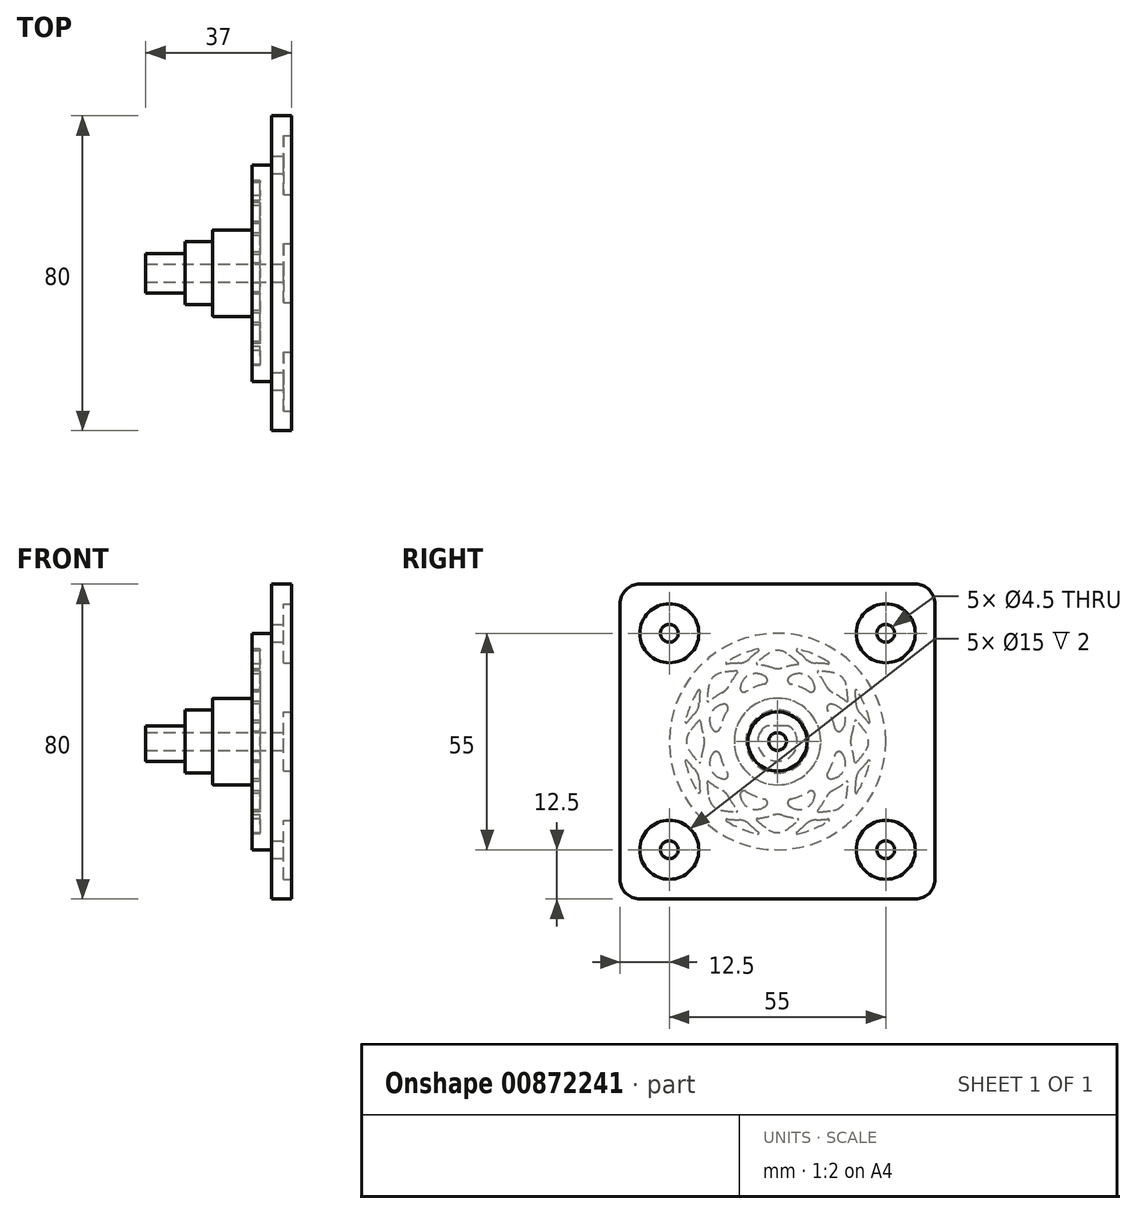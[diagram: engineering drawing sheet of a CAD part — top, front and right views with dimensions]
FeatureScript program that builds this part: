
annotation { "Feature Type Name" : "Feature", "Feature Type Description" : "" }
export const myFeature = defineFeature(function(context is Context, id is Id, definition is map)
    precondition{}
    {
        {
            var Q0;
            Q0=qCreatedBy(makeId("Right.planeOp"),FACE);
            var sketch = newSketch(context, id + "F0", { "sketchPlane" : qUnion([Q0])});
            skCircle(sketch, "E0", {"center": v(0, 0) * mm, "radius": 25 * mm, "construction": true});
            skCircle(sketch, "E1", {"center": v(0, 0) * mm, "radius": 15 * mm, "construction": true});
            skCircle(sketch, "E2", {"center": v(0, 0) * mm, "radius": 8 * mm});
            skArc(sketch, "E3", {"start": v(0, -25) * mm, "mid": v(15, 0) * mm, "end": v(0, 25) * mm, "construction": true});
            skArc(sketch, "E4", {"start": v(0, 25) * mm, "mid": v(-15, 0) * mm, "end": v(0, -25) * mm, "construction": true});
            skArc(sketch, "E5", {"start": v(25, 0) * mm, "mid": v(0, 15) * mm, "end": v(-25, 0) * mm, "construction": true});
            skArc(sketch, "E6", {"start": v(-25, 0) * mm, "mid": v(0, -15) * mm, "end": v(25, 0) * mm, "construction": true});
            skArc(sketch, "E7", {"start": v(17.68, -17.68) * mm, "mid": v(10.6, 10.6) * mm, "end": v(-17.68, 17.68) * mm, "construction": true});
            skArc(sketch, "E8", {"start": v(-17.68, 17.68) * mm, "mid": v(-10.6, -10.6) * mm, "end": v(17.68, -17.68) * mm, "construction": true});
            skArc(sketch, "E9", {"start": v(-17.68, -17.68) * mm, "mid": v(10.6, -10.6) * mm, "end": v(17.68, 17.68) * mm, "construction": true});
            skArc(sketch, "E10", {"start": v(17.68, 17.68) * mm, "mid": v(-10.6, 10.6) * mm, "end": v(-17.68, -17.68) * mm, "construction": true});
            skLineSegment(sketch, "E11", {"start": v(0, 25) * mm, "end": v(0, -25) * mm, "construction": true});
            skLineSegment(sketch, "E12", {"start": v(17.68, 17.68) * mm, "end": v(-17.68, -17.68) * mm, "construction": true});
            skLineSegment(sketch, "E13", {"start": v(-25, 0) * mm, "end": v(25, 0) * mm, "construction": true});
            skLineSegment(sketch, "E14", {"start": v(-17.68, 17.68) * mm, "end": v(17.68, -17.68) * mm, "construction": true});
            skCircle(sketch, "E15", {"center": v(0, 0) * mm, "radius": 27.5 * mm});
            skArc(sketch, "E16", {"start": v(-4, 23.66) * mm, "mid": v(-6.2, 21.88) * mm, "end": v(-8.23, 19.88) * mm});
            skArc(sketch, "E17", {"start": v(-8.23, 19.88) * mm, "mid": v(-11.08, 19.86) * mm, "end": v(-13.9, 19.56) * mm});
            skArc(sketch, "E18", {"start": v(8.23, 19.88) * mm, "mid": v(6.2, 21.88) * mm, "end": v(4, 23.66) * mm});
            skArc(sketch, "E19", {"start": v(16.87, 16.87) * mm, "mid": v(13.42, 17.61) * mm, "end": v(9.9, 17.9) * mm});
            skArc(sketch, "E20", {"start": v(12.97, 12.97) * mm, "mid": v(11.56, 15.51) * mm, "end": v(9.9, 17.9) * mm});
            skArc(sketch, "E21", {"start": v(-19.88, 8.23) * mm, "mid": v(-21.88, 6.2) * mm, "end": v(-23.66, 4) * mm});
            skArc(sketch, "E22", {"start": v(-19.56, 13.9) * mm, "mid": v(-19.86, 11.08) * mm, "end": v(-19.88, 8.23) * mm});
            skArc(sketch, "E23", {"start": v(19.88, 8.23) * mm, "mid": v(19.86, 11.08) * mm, "end": v(19.56, 13.9) * mm});
            skCircle(sketch, "E24", {"center": v(0, 0) * mm, "radius": 11 * mm});
            skArc(sketch, "E25", {"start": v(7.81, 18.86) * mm, "mid": v(4.25, 17.18) * mm, "end": v(1, 14.97) * mm});
            skArc(sketch, "E26", {"start": v(9.88, 11.3) * mm, "mid": v(9.14, 15.16) * mm, "end": v(7.81, 18.86) * mm});
            skArc(sketch, "E27", {"start": v(9.88, 11.3) * mm, "mid": v(5.74, 13.86) * mm, "end": v(1, 14.97) * mm});
            skArc(sketch, "E28", {"start": v(14.97, 1) * mm, "mid": v(17.18, 4.25) * mm, "end": v(18.86, 7.81) * mm});
            skArc(sketch, "E29", {"start": v(18.86, 7.81) * mm, "mid": v(15.16, 9.14) * mm, "end": v(11.3, 9.88) * mm});
            skArc(sketch, "E30", {"start": v(14.97, 1) * mm, "mid": v(13.86, 5.74) * mm, "end": v(11.3, 9.88) * mm});
            skArc(sketch, "E31", {"start": v(-19.66, 5.65) * mm, "mid": v(-21.94, 2.96) * mm, "end": v(-23.86, 0) * mm});
            skArc(sketch, "E32", {"start": v(-23.86, 0) * mm, "mid": v(-21.94, -2.96) * mm, "end": v(-19.66, -5.65) * mm});
            skArc(sketch, "E33", {"start": v(-18.35, 0) * mm, "mid": v(-19.15, -2.8) * mm, "end": v(-19.66, -5.65) * mm});
            skArc(sketch, "E34", {"start": v(23.86, 0) * mm, "mid": v(21.94, 2.96) * mm, "end": v(19.66, 5.65) * mm});
            skArc(sketch, "E35", {"start": v(18.35, 0) * mm, "mid": v(19.15, 2.8) * mm, "end": v(19.66, 5.65) * mm});
            skArc(sketch, "E36", {"start": v(-23.66, -4) * mm, "mid": v(-21.88, -6.2) * mm, "end": v(-19.88, -8.23) * mm});
            skArc(sketch, "E37", {"start": v(-19.88, -8.23) * mm, "mid": v(-19.86, -11.08) * mm, "end": v(-19.56, -13.9) * mm});
            skArc(sketch, "E38", {"start": v(19.88, -8.23) * mm, "mid": v(21.88, -6.2) * mm, "end": v(23.66, -4) * mm});
            skArc(sketch, "E39", {"start": v(19.56, -13.9) * mm, "mid": v(19.86, -11.08) * mm, "end": v(19.88, -8.23) * mm});
            skArc(sketch, "E40", {"start": v(12.97, -12.97) * mm, "mid": v(15.51, -11.56) * mm, "end": v(17.9, -9.9) * mm});
            skArc(sketch, "E41", {"start": v(16.87, -16.87) * mm, "mid": v(17.61, -13.42) * mm, "end": v(17.9, -9.9) * mm});
            skArc(sketch, "E42", {"start": v(-16.87, 16.87) * mm, "mid": v(-17.61, 13.42) * mm, "end": v(-17.9, 9.9) * mm});
            skArc(sketch, "E43", {"start": v(-9.9, 17.9) * mm, "mid": v(-11.56, 15.51) * mm, "end": v(-12.97, 12.97) * mm});
            skArc(sketch, "E44", {"start": v(-9.9, 17.9) * mm, "mid": v(-13.42, 17.61) * mm, "end": v(-16.87, 16.87) * mm});
            skArc(sketch, "E45", {"start": v(-14.97, -1) * mm, "mid": v(-17.18, -4.25) * mm, "end": v(-18.86, -7.81) * mm});
            skArc(sketch, "E46", {"start": v(-18.86, -7.81) * mm, "mid": v(-15.16, -9.14) * mm, "end": v(-11.3, -9.88) * mm});
            skArc(sketch, "E47", {"start": v(-18.86, 7.81) * mm, "mid": v(-17.18, 4.25) * mm, "end": v(-14.97, 1) * mm});
            skArc(sketch, "E48", {"start": v(-11.3, 9.88) * mm, "mid": v(-15.16, 9.14) * mm, "end": v(-18.86, 7.81) * mm});
            skArc(sketch, "E49", {"start": v(-1, 14.97) * mm, "mid": v(-4.25, 17.18) * mm, "end": v(-7.81, 18.86) * mm});
            skArc(sketch, "E50", {"start": v(-7.81, 18.86) * mm, "mid": v(-9.14, 15.16) * mm, "end": v(-9.88, 11.3) * mm});
            skArc(sketch, "E51", {"start": v(-1, 14.97) * mm, "mid": v(-5.74, 13.86) * mm, "end": v(-9.88, 11.3) * mm});
            skArc(sketch, "E52", {"start": v(1, -14.97) * mm, "mid": v(4.25, -17.18) * mm, "end": v(7.81, -18.86) * mm});
            skArc(sketch, "E53", {"start": v(7.81, -18.86) * mm, "mid": v(9.14, -15.16) * mm, "end": v(9.88, -11.3) * mm});
            skArc(sketch, "E54", {"start": v(1, -14.97) * mm, "mid": v(5.74, -13.86) * mm, "end": v(9.88, -11.3) * mm});
            skArc(sketch, "E55", {"start": v(-11.3, 9.88) * mm, "mid": v(-13.86, 5.74) * mm, "end": v(-14.97, 1) * mm});
            skArc(sketch, "E56", {"start": v(-9.88, -11.3) * mm, "mid": v(-9.14, -15.16) * mm, "end": v(-7.81, -18.86) * mm});
            skArc(sketch, "E57", {"start": v(-9.88, -11.3) * mm, "mid": v(-5.74, -13.86) * mm, "end": v(-1, -14.97) * mm});
            skArc(sketch, "E58", {"start": v(18.86, -7.81) * mm, "mid": v(17.18, -4.25) * mm, "end": v(14.97, -1) * mm});
            skArc(sketch, "E59", {"start": v(11.3, -9.88) * mm, "mid": v(15.16, -9.14) * mm, "end": v(18.86, -7.81) * mm});
            skArc(sketch, "E60", {"start": v(11.3, -9.88) * mm, "mid": v(13.86, -5.74) * mm, "end": v(14.97, -1) * mm});
            skArc(sketch, "E61", {"start": v(-7.81, -18.86) * mm, "mid": v(-4.25, -17.18) * mm, "end": v(-1, -14.97) * mm});
            skArc(sketch, "E62", {"start": v(-19.66, 5.65) * mm, "mid": v(-19.15, 2.8) * mm, "end": v(-18.35, 0) * mm});
            skArc(sketch, "E63", {"start": v(-13.9, -19.56) * mm, "mid": v(-11.08, -19.86) * mm, "end": v(-8.23, -19.88) * mm});
            skArc(sketch, "E64", {"start": v(-8.23, -19.88) * mm, "mid": v(-6.2, -21.88) * mm, "end": v(-4, -23.66) * mm});
            skArc(sketch, "E65", {"start": v(-12.97, 12.97) * mm, "mid": v(-15.51, 11.56) * mm, "end": v(-17.9, 9.9) * mm});
            skArc(sketch, "E66", {"start": v(-17.9, -9.9) * mm, "mid": v(-15.51, -11.56) * mm, "end": v(-12.97, -12.97) * mm});
            skArc(sketch, "E67", {"start": v(-17.9, -9.9) * mm, "mid": v(-17.61, -13.42) * mm, "end": v(-16.87, -16.87) * mm});
            skArc(sketch, "E68", {"start": v(-16.87, -16.87) * mm, "mid": v(-13.42, -17.61) * mm, "end": v(-9.9, -17.9) * mm});
            skArc(sketch, "E69", {"start": v(-12.97, -12.97) * mm, "mid": v(-11.56, -15.51) * mm, "end": v(-9.9, -17.9) * mm});
            skArc(sketch, "E70", {"start": v(-5.65, -19.66) * mm, "mid": v(-2.8, -19.15) * mm, "end": v(0, -18.35) * mm});
            skArc(sketch, "E71", {"start": v(-5.65, -19.66) * mm, "mid": v(-2.96, -21.94) * mm, "end": v(0, -23.86) * mm});
            skArc(sketch, "E72", {"start": v(0, -18.35) * mm, "mid": v(2.8, -19.15) * mm, "end": v(5.65, -19.66) * mm});
            skArc(sketch, "E73", {"start": v(0, -23.86) * mm, "mid": v(2.96, -21.94) * mm, "end": v(5.65, -19.66) * mm});
            skArc(sketch, "E74", {"start": v(4, -23.66) * mm, "mid": v(6.2, -21.88) * mm, "end": v(8.23, -19.88) * mm});
            skArc(sketch, "E75", {"start": v(8.23, -19.88) * mm, "mid": v(11.08, -19.86) * mm, "end": v(13.9, -19.56) * mm});
            skArc(sketch, "E76", {"start": v(0, 23.86) * mm, "mid": v(-2.96, 21.94) * mm, "end": v(-5.65, 19.66) * mm});
            skArc(sketch, "E77", {"start": v(0, 18.35) * mm, "mid": v(-2.8, 19.15) * mm, "end": v(-5.65, 19.66) * mm});
            skArc(sketch, "E78", {"start": v(5.65, 19.66) * mm, "mid": v(2.96, 21.94) * mm, "end": v(0, 23.86) * mm});
            skArc(sketch, "E79", {"start": v(5.65, 19.66) * mm, "mid": v(2.8, 19.15) * mm, "end": v(0, 18.35) * mm});
            skArc(sketch, "E80", {"start": v(17.9, 9.9) * mm, "mid": v(15.51, 11.56) * mm, "end": v(12.97, 12.97) * mm});
            skArc(sketch, "E81", {"start": v(17.9, 9.9) * mm, "mid": v(17.61, 13.42) * mm, "end": v(16.87, 16.87) * mm});
            skArc(sketch, "E82", {"start": v(19.66, -5.65) * mm, "mid": v(21.94, -2.96) * mm, "end": v(23.86, 0) * mm});
            skArc(sketch, "E83", {"start": v(19.66, -5.65) * mm, "mid": v(19.15, -2.8) * mm, "end": v(18.35, 0) * mm});
            skArc(sketch, "E84", {"start": v(9.9, -17.9) * mm, "mid": v(11.56, -15.51) * mm, "end": v(12.97, -12.97) * mm});
            skArc(sketch, "E85", {"start": v(9.9, -17.9) * mm, "mid": v(13.42, -17.61) * mm, "end": v(16.87, -16.87) * mm});
            skArc(sketch, "E86", {"start": v(-14.97, -1) * mm, "mid": v(-13.86, -5.74) * mm, "end": v(-11.3, -9.88) * mm});
            skArc(sketch, "E87", {"start": v(-19.56, 13.9) * mm, "mid": v(-22.17, 9.18) * mm, "end": v(-23.66, 4) * mm});
            skCircle(sketch, "E88", {"center": v(0, 0) * mm, "radius": 24 * mm, "construction": true});
            skArc(sketch, "E89", {"start": v(-4, 23.66) * mm, "mid": v(-9.18, 22.17) * mm, "end": v(-13.9, 19.56) * mm});
            skArc(sketch, "E90", {"start": v(23.66, 4) * mm, "mid": v(21.88, 6.2) * mm, "end": v(19.88, 8.23) * mm});
            skArc(sketch, "E91", {"start": v(23.66, 4) * mm, "mid": v(22.17, 9.18) * mm, "end": v(19.56, 13.9) * mm});
            skArc(sketch, "E92", {"start": v(13.9, 19.56) * mm, "mid": v(11.08, 19.86) * mm, "end": v(8.23, 19.88) * mm});
            skArc(sketch, "E93", {"start": v(13.9, 19.56) * mm, "mid": v(9.18, 22.17) * mm, "end": v(4, 23.66) * mm});
            skArc(sketch, "E94", {"start": v(-23.66, -4) * mm, "mid": v(-22.17, -9.18) * mm, "end": v(-19.56, -13.9) * mm});
            skArc(sketch, "E95", {"start": v(-13.9, -19.56) * mm, "mid": v(-9.18, -22.17) * mm, "end": v(-4, -23.66) * mm});
            skArc(sketch, "E96", {"start": v(4, -23.66) * mm, "mid": v(9.18, -22.17) * mm, "end": v(13.9, -19.56) * mm});
            skArc(sketch, "E97", {"start": v(19.56, -13.9) * mm, "mid": v(22.17, -9.18) * mm, "end": v(23.66, -4) * mm});
            skSolve(sketch);
        }
        {
            var Q0;
            Q0=qCreatedBy(makeId("Right.planeOp"),FACE);
            var sketch = newSketch(context, id + "F1", { "sketchPlane" : qUnion([Q0])});
            skCircle(sketch, "E98", {"center": v(0, 0) * mm, "radius": 27.5 * mm});
            skSolve(sketch);
        }
        {
            var Q0;
            Q0 = qSketchRegion(id + "F1", true);
            extrude(context, id + "F2", {"entities" : qUnion([Q0]), "depth" : 5 * mm, "offsetDistance" : 25 * mm});
        }
        {
            var Q0;
            Q0=makeQuery(id+"F2.opExtrude","CAP_FACE",FACE,{"disambiguationData":[OSD([sQuery(id+"F1.wireOp",EDGE,"E98")])],"isStart":false});
            var sketch = newSketch(context, id + "F3", { "sketchPlane" : qUnion([Q0])});
            skLineSegment(sketch, "E99.bottom", {"start": v(40, -40) * mm, "end": v(-40, -40) * mm});
            skLineSegment(sketch, "E99.top", {"start": v(40, 40) * mm, "end": v(-40, 40) * mm});
            skLineSegment(sketch, "E99.left", {"start": v(40, -40) * mm, "end": v(40, 40) * mm});
            skLineSegment(sketch, "E99.right", {"start": v(-40, -40) * mm, "end": v(-40, 40) * mm});
            skPoint(sketch, "E99.middle", {"position": v(0, 0) * mm});
            skSolve(sketch);
        }
        {
            var Q0;
            Q0=makeQuery(id+"F3.imprint","IMPRINT",FACE,{"disambiguationData":[TD([[makeQuery(id+"F3.imprint","IMPRINT",EDGE,{"derivedFrom":sQuery(id+"F3.wireOp",EDGE,"E99.bottom")}),-1.0]])]});
            var Q1;
            Q1=makeQuery(id+"F3.imprint","IMPRINT",FACE,{"disambiguationData":[TD([[makeQuery(id+"F3.imprint","IMPRINT",EDGE,{"derivedFrom":makeQuery(id+"F2.opExtrude","CAP_EDGE",EDGE,{"disambiguationData":[OSD([sQuery(id+"F1.wireOp",EDGE,"E98")])],"isStart":false})}),1.0]])]});
            extrude(context, id + "F4", {"entities" : qUnion([Q0, Q1]), "operationType" : NewBodyOperationType.ADD, "depth" : 5 * mm, "offsetDistance" : 25 * mm});
        }
        {
            var Q0;
            Q0=makeQuery(id+"F0.imprint","IMPRINT",FACE,{"disambiguationData":[TD([[makeQuery(id+"F0.imprint","IMPRINT",EDGE,{"derivedFrom":sQuery(id+"F0.wireOp",EDGE,"E21")}),-1.0]])]});
            var Q1;
            Q1=makeQuery(id+"F0.imprint","IMPRINT",FACE,{"disambiguationData":[TD([[makeQuery(id+"F0.imprint","IMPRINT",EDGE,{"derivedFrom":sQuery(id+"F0.wireOp",EDGE,"E31")}),1.0]])]});
            var Q2;
            Q2=makeQuery(id+"F0.imprint","IMPRINT",FACE,{"disambiguationData":[TD([[makeQuery(id+"F0.imprint","IMPRINT",EDGE,{"derivedFrom":sQuery(id+"F0.wireOp",EDGE,"E47")}),1.0]])]});
            var Q3;
            Q3=makeQuery(id+"F0.imprint","IMPRINT",FACE,{"disambiguationData":[TD([[makeQuery(id+"F0.imprint","IMPRINT",EDGE,{"derivedFrom":sQuery(id+"F0.wireOp",EDGE,"E42")}),1.0]])]});
            var Q4;
            Q4=makeQuery(id+"F0.imprint","IMPRINT",FACE,{"disambiguationData":[TD([[makeQuery(id+"F0.imprint","IMPRINT",EDGE,{"derivedFrom":sQuery(id+"F0.wireOp",EDGE,"E16")}),-1.0]])]});
            var Q5;
            Q5=makeQuery(id+"F0.imprint","IMPRINT",FACE,{"disambiguationData":[TD([[makeQuery(id+"F0.imprint","IMPRINT",EDGE,{"derivedFrom":sQuery(id+"F0.wireOp",EDGE,"E49")}),1.0]])]});
            var Q6;
            Q6=makeQuery(id+"F0.imprint","IMPRINT",FACE,{"disambiguationData":[TD([[makeQuery(id+"F0.imprint","IMPRINT",EDGE,{"derivedFrom":sQuery(id+"F0.wireOp",EDGE,"E76")}),1.0]])]});
            var Q7;
            Q7=makeQuery(id+"F0.imprint","IMPRINT",FACE,{"disambiguationData":[TD([[makeQuery(id+"F0.imprint","IMPRINT",EDGE,{"derivedFrom":sQuery(id+"F0.wireOp",EDGE,"E18")}),-1.0]])]});
            var Q8;
            Q8=makeQuery(id+"F0.imprint","IMPRINT",FACE,{"disambiguationData":[TD([[makeQuery(id+"F0.imprint","IMPRINT",EDGE,{"derivedFrom":sQuery(id+"F0.wireOp",EDGE,"E25")}),1.0]])]});
            var Q9;
            Q9=makeQuery(id+"F0.imprint","IMPRINT",FACE,{"disambiguationData":[TD([[makeQuery(id+"F0.imprint","IMPRINT",EDGE,{"derivedFrom":sQuery(id+"F0.wireOp",EDGE,"E19")}),1.0]])]});
            var Q10;
            Q10=makeQuery(id+"F0.imprint","IMPRINT",FACE,{"disambiguationData":[TD([[makeQuery(id+"F0.imprint","IMPRINT",EDGE,{"derivedFrom":sQuery(id+"F0.wireOp",EDGE,"E23")}),-1.0]])]});
            var Q11;
            Q11=makeQuery(id+"F0.imprint","IMPRINT",FACE,{"disambiguationData":[TD([[makeQuery(id+"F0.imprint","IMPRINT",EDGE,{"derivedFrom":sQuery(id+"F0.wireOp",EDGE,"E28")}),1.0]])]});
            var Q12;
            Q12=makeQuery(id+"F0.imprint","IMPRINT",FACE,{"disambiguationData":[TD([[makeQuery(id+"F0.imprint","IMPRINT",EDGE,{"derivedFrom":sQuery(id+"F0.wireOp",EDGE,"E34")}),1.0]])]});
            var Q13;
            Q13=makeQuery(id+"F0.imprint","IMPRINT",FACE,{"disambiguationData":[TD([[makeQuery(id+"F0.imprint","IMPRINT",EDGE,{"derivedFrom":sQuery(id+"F0.wireOp",EDGE,"E58")}),1.0]])]});
            var Q14;
            Q14=makeQuery(id+"F0.imprint","IMPRINT",FACE,{"disambiguationData":[TD([[makeQuery(id+"F0.imprint","IMPRINT",EDGE,{"derivedFrom":sQuery(id+"F0.wireOp",EDGE,"E40")}),-1.0]])]});
            var Q15;
            Q15=makeQuery(id+"F0.imprint","IMPRINT",FACE,{"disambiguationData":[TD([[makeQuery(id+"F0.imprint","IMPRINT",EDGE,{"derivedFrom":sQuery(id+"F0.wireOp",EDGE,"E38")}),-1.0]])]});
            var Q16;
            Q16=makeQuery(id+"F0.imprint","IMPRINT",FACE,{"disambiguationData":[TD([[makeQuery(id+"F0.imprint","IMPRINT",EDGE,{"derivedFrom":sQuery(id+"F0.wireOp",EDGE,"E74")}),-1.0]])]});
            var Q17;
            Q17=makeQuery(id+"F0.imprint","IMPRINT",FACE,{"disambiguationData":[TD([[makeQuery(id+"F0.imprint","IMPRINT",EDGE,{"derivedFrom":sQuery(id+"F0.wireOp",EDGE,"E52")}),1.0]])]});
            var Q18;
            Q18=makeQuery(id+"F0.imprint","IMPRINT",FACE,{"disambiguationData":[TD([[makeQuery(id+"F0.imprint","IMPRINT",EDGE,{"derivedFrom":sQuery(id+"F0.wireOp",EDGE,"E70")}),-1.0]])]});
            var Q19;
            Q19=makeQuery(id+"F0.imprint","IMPRINT",FACE,{"disambiguationData":[TD([[makeQuery(id+"F0.imprint","IMPRINT",EDGE,{"derivedFrom":sQuery(id+"F0.wireOp",EDGE,"E56")}),1.0]])]});
            var Q20;
            Q20=makeQuery(id+"F0.imprint","IMPRINT",FACE,{"disambiguationData":[TD([[makeQuery(id+"F0.imprint","IMPRINT",EDGE,{"derivedFrom":sQuery(id+"F0.wireOp",EDGE,"E63")}),-1.0]])]});
            var Q21;
            Q21=makeQuery(id+"F0.imprint","IMPRINT",FACE,{"disambiguationData":[TD([[makeQuery(id+"F0.imprint","IMPRINT",EDGE,{"derivedFrom":sQuery(id+"F0.wireOp",EDGE,"E66")}),-1.0]])]});
            var Q22;
            Q22=makeQuery(id+"F0.imprint","IMPRINT",FACE,{"disambiguationData":[TD([[makeQuery(id+"F0.imprint","IMPRINT",EDGE,{"derivedFrom":sQuery(id+"F0.wireOp",EDGE,"E36")}),-1.0]])]});
            var Q23;
            Q23=makeQuery(id+"F0.imprint","IMPRINT",FACE,{"disambiguationData":[TD([[makeQuery(id+"F0.imprint","IMPRINT",EDGE,{"derivedFrom":sQuery(id+"F0.wireOp",EDGE,"E45")}),1.0]])]});
            extrude(context, id + "F5", {"entities" : qUnion([Q0, Q1, Q2, Q3, Q4, Q5, Q6, Q7, Q8, Q9, Q10, Q11, Q12, Q13, Q14, Q15, Q16, Q17, Q18, Q19, Q20, Q21, Q22, Q23]), "operationType" : NewBodyOperationType.REMOVE, "depth" : 2 * mm, "offsetDistance" : 25 * mm});
        }
        {
            var Q0;
            Q0=makeQuery(id+"F5.boolean.opBoolean","COPY",EDGE,{"derivedFrom":makeQuery(id+"F5.opExtrude","SWEPT_EDGE",EDGE,{"disambiguationData":[OSD([sQuery(id+"F0.wireOp",EDGE,"E28"),sQuery(id+"F0.wireOp",EDGE,"E29")])]})});
            var Q1;
            Q1=makeQuery(id+"F5.boolean.opBoolean","COPY",EDGE,{"derivedFrom":makeQuery(id+"F5.opExtrude","SWEPT_EDGE",EDGE,{"disambiguationData":[OSD([sQuery(id+"F0.wireOp",EDGE,"E23"),sQuery(id+"F0.wireOp",EDGE,"E90")])]})});
            var Q2;
            Q2=makeQuery(id+"F5.boolean.opBoolean","COPY",EDGE,{"derivedFrom":makeQuery(id+"F5.opExtrude","SWEPT_EDGE",EDGE,{"disambiguationData":[OSD([sQuery(id+"F0.wireOp",EDGE,"E18"),sQuery(id+"F0.wireOp",EDGE,"E92")])]})});
            var Q3;
            Q3=makeQuery(id+"F5.boolean.opBoolean","COPY",EDGE,{"derivedFrom":makeQuery(id+"F5.opExtrude","SWEPT_EDGE",EDGE,{"disambiguationData":[OSD([sQuery(id+"F0.wireOp",EDGE,"E25"),sQuery(id+"F0.wireOp",EDGE,"E26")])]})});
            var Q4;
            Q4=makeQuery(id+"F5.boolean.opBoolean","COPY",EDGE,{"derivedFrom":makeQuery(id+"F5.opExtrude","SWEPT_EDGE",EDGE,{"disambiguationData":[OSD([sQuery(id+"F0.wireOp",EDGE,"E49"),sQuery(id+"F0.wireOp",EDGE,"E50")])]})});
            var Q5;
            Q5=makeQuery(id+"F5.boolean.opBoolean","COPY",EDGE,{"derivedFrom":makeQuery(id+"F5.opExtrude","SWEPT_EDGE",EDGE,{"disambiguationData":[OSD([sQuery(id+"F0.wireOp",EDGE,"E16"),sQuery(id+"F0.wireOp",EDGE,"E17")])]})});
            var Q6;
            Q6=makeQuery(id+"F5.boolean.opBoolean","COPY",EDGE,{"derivedFrom":makeQuery(id+"F5.opExtrude","SWEPT_EDGE",EDGE,{"disambiguationData":[OSD([sQuery(id+"F0.wireOp",EDGE,"E21"),sQuery(id+"F0.wireOp",EDGE,"E22")])]})});
            var Q7;
            Q7=makeQuery(id+"F5.boolean.opBoolean","COPY",EDGE,{"derivedFrom":makeQuery(id+"F5.opExtrude","SWEPT_EDGE",EDGE,{"disambiguationData":[OSD([sQuery(id+"F0.wireOp",EDGE,"E47"),sQuery(id+"F0.wireOp",EDGE,"E48")])]})});
            var Q8;
            Q8=makeQuery(id+"F5.boolean.opBoolean","COPY",EDGE,{"derivedFrom":makeQuery(id+"F5.opExtrude","SWEPT_EDGE",EDGE,{"disambiguationData":[OSD([sQuery(id+"F0.wireOp",EDGE,"E45"),sQuery(id+"F0.wireOp",EDGE,"E46")])]})});
            var Q9;
            Q9=makeQuery(id+"F5.boolean.opBoolean","COPY",EDGE,{"derivedFrom":makeQuery(id+"F5.opExtrude","SWEPT_EDGE",EDGE,{"disambiguationData":[OSD([sQuery(id+"F0.wireOp",EDGE,"E36"),sQuery(id+"F0.wireOp",EDGE,"E37")])]})});
            var Q10;
            Q10=makeQuery(id+"F5.boolean.opBoolean","COPY",EDGE,{"derivedFrom":makeQuery(id+"F5.opExtrude","SWEPT_EDGE",EDGE,{"disambiguationData":[OSD([sQuery(id+"F0.wireOp",EDGE,"E56"),sQuery(id+"F0.wireOp",EDGE,"E61")])]})});
            var Q11;
            Q11=makeQuery(id+"F5.boolean.opBoolean","COPY",EDGE,{"derivedFrom":makeQuery(id+"F5.opExtrude","SWEPT_EDGE",EDGE,{"disambiguationData":[OSD([sQuery(id+"F0.wireOp",EDGE,"E63"),sQuery(id+"F0.wireOp",EDGE,"E64")])]})});
            var Q12;
            Q12=makeQuery(id+"F5.boolean.opBoolean","COPY",EDGE,{"derivedFrom":makeQuery(id+"F5.opExtrude","SWEPT_EDGE",EDGE,{"disambiguationData":[OSD([sQuery(id+"F0.wireOp",EDGE,"E52"),sQuery(id+"F0.wireOp",EDGE,"E53")])]})});
            var Q13;
            Q13=makeQuery(id+"F5.boolean.opBoolean","COPY",EDGE,{"derivedFrom":makeQuery(id+"F5.opExtrude","SWEPT_EDGE",EDGE,{"disambiguationData":[OSD([sQuery(id+"F0.wireOp",EDGE,"E74"),sQuery(id+"F0.wireOp",EDGE,"E75")])]})});
            var Q14;
            Q14=makeQuery(id+"F5.boolean.opBoolean","COPY",EDGE,{"derivedFrom":makeQuery(id+"F5.opExtrude","SWEPT_EDGE",EDGE,{"disambiguationData":[OSD([sQuery(id+"F0.wireOp",EDGE,"E38"),sQuery(id+"F0.wireOp",EDGE,"E39")])]})});
            var Q15;
            Q15=makeQuery(id+"F5.boolean.opBoolean","COPY",EDGE,{"derivedFrom":makeQuery(id+"F5.opExtrude","SWEPT_EDGE",EDGE,{"disambiguationData":[OSD([sQuery(id+"F0.wireOp",EDGE,"E58"),sQuery(id+"F0.wireOp",EDGE,"E59")])]})});
            var Q16;
            Q16=makeQuery(id+"F5.boolean.opBoolean","COPY",EDGE,{"derivedFrom":makeQuery(id+"F5.opExtrude","SWEPT_EDGE",EDGE,{"disambiguationData":[OSD([sQuery(id+"F0.wireOp",EDGE,"E35"),sQuery(id+"F0.wireOp",EDGE,"E83")])]})});
            var Q17;
            Q17=makeQuery(id+"F5.boolean.opBoolean","COPY",EDGE,{"derivedFrom":makeQuery(id+"F5.opExtrude","SWEPT_EDGE",EDGE,{"disambiguationData":[OSD([sQuery(id+"F0.wireOp",EDGE,"E34"),sQuery(id+"F0.wireOp",EDGE,"E82")])]})});
            var Q18;
            Q18=makeQuery(id+"F5.boolean.opBoolean","COPY",EDGE,{"derivedFrom":makeQuery(id+"F5.opExtrude","SWEPT_EDGE",EDGE,{"disambiguationData":[OSD([sQuery(id+"F0.wireOp",EDGE,"E41"),sQuery(id+"F0.wireOp",EDGE,"E85")])]})});
            var Q19;
            Q19=makeQuery(id+"F5.boolean.opBoolean","COPY",EDGE,{"derivedFrom":makeQuery(id+"F5.opExtrude","SWEPT_EDGE",EDGE,{"disambiguationData":[OSD([sQuery(id+"F0.wireOp",EDGE,"E40"),sQuery(id+"F0.wireOp",EDGE,"E84")])]})});
            var Q20;
            Q20=makeQuery(id+"F5.boolean.opBoolean","COPY",EDGE,{"derivedFrom":makeQuery(id+"F5.opExtrude","SWEPT_EDGE",EDGE,{"disambiguationData":[OSD([sQuery(id+"F0.wireOp",EDGE,"E70"),sQuery(id+"F0.wireOp",EDGE,"E72")])]})});
            var Q21;
            Q21=makeQuery(id+"F5.boolean.opBoolean","COPY",EDGE,{"derivedFrom":makeQuery(id+"F5.opExtrude","SWEPT_EDGE",EDGE,{"disambiguationData":[OSD([sQuery(id+"F0.wireOp",EDGE,"E71"),sQuery(id+"F0.wireOp",EDGE,"E73")])]})});
            var Q22;
            Q22=makeQuery(id+"F5.boolean.opBoolean","COPY",EDGE,{"derivedFrom":makeQuery(id+"F5.opExtrude","SWEPT_EDGE",EDGE,{"disambiguationData":[OSD([sQuery(id+"F0.wireOp",EDGE,"E67"),sQuery(id+"F0.wireOp",EDGE,"E68")])]})});
            var Q23;
            Q23=makeQuery(id+"F5.boolean.opBoolean","COPY",EDGE,{"derivedFrom":makeQuery(id+"F5.opExtrude","SWEPT_EDGE",EDGE,{"disambiguationData":[OSD([sQuery(id+"F0.wireOp",EDGE,"E66"),sQuery(id+"F0.wireOp",EDGE,"E69")])]})});
            var Q24;
            Q24=makeQuery(id+"F5.boolean.opBoolean","COPY",EDGE,{"derivedFrom":makeQuery(id+"F5.opExtrude","SWEPT_EDGE",EDGE,{"disambiguationData":[OSD([sQuery(id+"F0.wireOp",EDGE,"E33"),sQuery(id+"F0.wireOp",EDGE,"E62")])]})});
            var Q25;
            Q25=makeQuery(id+"F5.boolean.opBoolean","COPY",EDGE,{"derivedFrom":makeQuery(id+"F5.opExtrude","SWEPT_EDGE",EDGE,{"disambiguationData":[OSD([sQuery(id+"F0.wireOp",EDGE,"E31"),sQuery(id+"F0.wireOp",EDGE,"E32")])]})});
            var Q26;
            Q26=makeQuery(id+"F5.boolean.opBoolean","COPY",EDGE,{"derivedFrom":makeQuery(id+"F5.opExtrude","SWEPT_EDGE",EDGE,{"disambiguationData":[OSD([sQuery(id+"F0.wireOp",EDGE,"E42"),sQuery(id+"F0.wireOp",EDGE,"E44")])]})});
            var Q27;
            Q27=makeQuery(id+"F5.boolean.opBoolean","COPY",EDGE,{"derivedFrom":makeQuery(id+"F5.opExtrude","SWEPT_EDGE",EDGE,{"disambiguationData":[OSD([sQuery(id+"F0.wireOp",EDGE,"E43"),sQuery(id+"F0.wireOp",EDGE,"E65")])]})});
            var Q28;
            Q28=makeQuery(id+"F5.boolean.opBoolean","COPY",EDGE,{"derivedFrom":makeQuery(id+"F5.opExtrude","SWEPT_EDGE",EDGE,{"disambiguationData":[OSD([sQuery(id+"F0.wireOp",EDGE,"E77"),sQuery(id+"F0.wireOp",EDGE,"E79")])]})});
            var Q29;
            Q29=makeQuery(id+"F5.boolean.opBoolean","COPY",EDGE,{"derivedFrom":makeQuery(id+"F5.opExtrude","SWEPT_EDGE",EDGE,{"disambiguationData":[OSD([sQuery(id+"F0.wireOp",EDGE,"E76"),sQuery(id+"F0.wireOp",EDGE,"E78")])]})});
            var Q30;
            Q30=makeQuery(id+"F5.boolean.opBoolean","COPY",EDGE,{"derivedFrom":makeQuery(id+"F5.opExtrude","SWEPT_EDGE",EDGE,{"disambiguationData":[OSD([sQuery(id+"F0.wireOp",EDGE,"E20"),sQuery(id+"F0.wireOp",EDGE,"E80")])]})});
            var Q31;
            Q31=makeQuery(id+"F5.boolean.opBoolean","COPY",EDGE,{"derivedFrom":makeQuery(id+"F5.opExtrude","SWEPT_EDGE",EDGE,{"disambiguationData":[OSD([sQuery(id+"F0.wireOp",EDGE,"E19"),sQuery(id+"F0.wireOp",EDGE,"E81")])]})});
            fillet(context, id + "F6", {"entities" : qUnion([Q0, Q1, Q2, Q3, Q4, Q5, Q6, Q7, Q8, Q9, Q10, Q11, Q12, Q13, Q14, Q15, Q16, Q17, Q18, Q19, Q20, Q21, Q22, Q23, Q24, Q25, Q26, Q27, Q28, Q29, Q30, Q31]), "radius" : 4 * mm, "tangentPropagation" : true, "defaultsChanged" : false, "vertexSettings" : [], "allowEdgeOverflow" : false});
        }
        {
            var Q0;
            Q0=makeQuery(id+"F5.boolean.opBoolean","COPY",EDGE,{"derivedFrom":makeQuery(id+"F5.opExtrude","SWEPT_EDGE",EDGE,{"disambiguationData":[OSD([sQuery(id+"F0.wireOp",EDGE,"E58"),sQuery(id+"F0.wireOp",EDGE,"E60")])]})});
            var Q1;
            Q1=makeQuery(id+"F5.boolean.opBoolean","COPY",EDGE,{"derivedFrom":makeQuery(id+"F5.opExtrude","SWEPT_EDGE",EDGE,{"disambiguationData":[OSD([sQuery(id+"F0.wireOp",EDGE,"E28"),sQuery(id+"F0.wireOp",EDGE,"E30")])]})});
            var Q2;
            Q2=makeQuery(id+"F5.boolean.opBoolean","COPY",EDGE,{"derivedFrom":makeQuery(id+"F5.opExtrude","SWEPT_EDGE",EDGE,{"disambiguationData":[OSD([sQuery(id+"F0.wireOp",EDGE,"E29"),sQuery(id+"F0.wireOp",EDGE,"E30")])]})});
            var Q3;
            Q3=makeQuery(id+"F5.boolean.opBoolean","COPY",EDGE,{"derivedFrom":makeQuery(id+"F5.opExtrude","SWEPT_EDGE",EDGE,{"disambiguationData":[OSD([sQuery(id+"F0.wireOp",EDGE,"E26"),sQuery(id+"F0.wireOp",EDGE,"E27")])]})});
            var Q4;
            Q4=makeQuery(id+"F5.boolean.opBoolean","COPY",EDGE,{"derivedFrom":makeQuery(id+"F5.opExtrude","SWEPT_EDGE",EDGE,{"disambiguationData":[OSD([sQuery(id+"F0.wireOp",EDGE,"E25"),sQuery(id+"F0.wireOp",EDGE,"E27")])]})});
            var Q5;
            Q5=makeQuery(id+"F5.boolean.opBoolean","COPY",EDGE,{"derivedFrom":makeQuery(id+"F5.opExtrude","SWEPT_EDGE",EDGE,{"disambiguationData":[OSD([sQuery(id+"F0.wireOp",EDGE,"E49"),sQuery(id+"F0.wireOp",EDGE,"E51")])]})});
            var Q6;
            Q6=makeQuery(id+"F5.boolean.opBoolean","COPY",EDGE,{"derivedFrom":makeQuery(id+"F5.opExtrude","SWEPT_EDGE",EDGE,{"disambiguationData":[OSD([sQuery(id+"F0.wireOp",EDGE,"E50"),sQuery(id+"F0.wireOp",EDGE,"E51")])]})});
            var Q7;
            Q7=makeQuery(id+"F5.boolean.opBoolean","COPY",EDGE,{"derivedFrom":makeQuery(id+"F5.opExtrude","SWEPT_EDGE",EDGE,{"disambiguationData":[OSD([sQuery(id+"F0.wireOp",EDGE,"E48"),sQuery(id+"F0.wireOp",EDGE,"E55")])]})});
            var Q8;
            Q8=makeQuery(id+"F5.boolean.opBoolean","COPY",EDGE,{"derivedFrom":makeQuery(id+"F5.opExtrude","SWEPT_EDGE",EDGE,{"disambiguationData":[OSD([sQuery(id+"F0.wireOp",EDGE,"E47"),sQuery(id+"F0.wireOp",EDGE,"E55")])]})});
            var Q9;
            Q9=makeQuery(id+"F5.boolean.opBoolean","COPY",EDGE,{"derivedFrom":makeQuery(id+"F5.opExtrude","SWEPT_EDGE",EDGE,{"disambiguationData":[OSD([sQuery(id+"F0.wireOp",EDGE,"E45"),sQuery(id+"F0.wireOp",EDGE,"E86")])]})});
            var Q10;
            Q10=makeQuery(id+"F5.boolean.opBoolean","COPY",EDGE,{"derivedFrom":makeQuery(id+"F5.opExtrude","SWEPT_EDGE",EDGE,{"disambiguationData":[OSD([sQuery(id+"F0.wireOp",EDGE,"E46"),sQuery(id+"F0.wireOp",EDGE,"E86")])]})});
            var Q11;
            Q11=makeQuery(id+"F5.boolean.opBoolean","COPY",EDGE,{"derivedFrom":makeQuery(id+"F5.opExtrude","SWEPT_EDGE",EDGE,{"disambiguationData":[OSD([sQuery(id+"F0.wireOp",EDGE,"E56"),sQuery(id+"F0.wireOp",EDGE,"E57")])]})});
            var Q12;
            Q12=makeQuery(id+"F5.boolean.opBoolean","COPY",EDGE,{"derivedFrom":makeQuery(id+"F5.opExtrude","SWEPT_EDGE",EDGE,{"disambiguationData":[OSD([sQuery(id+"F0.wireOp",EDGE,"E57"),sQuery(id+"F0.wireOp",EDGE,"E61")])]})});
            var Q13;
            Q13=makeQuery(id+"F5.boolean.opBoolean","COPY",EDGE,{"derivedFrom":makeQuery(id+"F5.opExtrude","SWEPT_EDGE",EDGE,{"disambiguationData":[OSD([sQuery(id+"F0.wireOp",EDGE,"E52"),sQuery(id+"F0.wireOp",EDGE,"E54")])]})});
            var Q14;
            Q14=makeQuery(id+"F5.boolean.opBoolean","COPY",EDGE,{"derivedFrom":makeQuery(id+"F5.opExtrude","SWEPT_EDGE",EDGE,{"disambiguationData":[OSD([sQuery(id+"F0.wireOp",EDGE,"E53"),sQuery(id+"F0.wireOp",EDGE,"E54")])]})});
            var Q15;
            Q15=makeQuery(id+"F5.boolean.opBoolean","COPY",EDGE,{"derivedFrom":makeQuery(id+"F5.opExtrude","SWEPT_EDGE",EDGE,{"disambiguationData":[OSD([sQuery(id+"F0.wireOp",EDGE,"E59"),sQuery(id+"F0.wireOp",EDGE,"E60")])]})});
            fillet(context, id + "F7", {"entities" : qUnion([Q0, Q1, Q2, Q3, Q4, Q5, Q6, Q7, Q8, Q9, Q10, Q11, Q12, Q13, Q14, Q15]), "radius" : 1 * mm, "tangentPropagation" : true, "defaultsChanged" : false, "vertexSettings" : [], "allowEdgeOverflow" : false});
        }
        {
            var Q0;
            Q0=makeQuery(id+"F5.boolean.opBoolean","COPY",EDGE,{"derivedFrom":makeQuery(id+"F5.opExtrude","SWEPT_EDGE",EDGE,{"disambiguationData":[OSD([sQuery(id+"F0.wireOp",EDGE,"E19"),sQuery(id+"F0.wireOp",EDGE,"E20")])]})});
            var Q1;
            Q1=makeQuery(id+"F5.boolean.opBoolean","COPY",EDGE,{"derivedFrom":makeQuery(id+"F5.opExtrude","SWEPT_EDGE",EDGE,{"disambiguationData":[OSD([sQuery(id+"F0.wireOp",EDGE,"E18"),sQuery(id+"F0.wireOp",EDGE,"E93")])]})});
            var Q2;
            Q2=makeQuery(id+"F5.boolean.opBoolean","COPY",EDGE,{"derivedFrom":makeQuery(id+"F5.opExtrude","SWEPT_EDGE",EDGE,{"disambiguationData":[OSD([sQuery(id+"F0.wireOp",EDGE,"E92"),sQuery(id+"F0.wireOp",EDGE,"E93")])]})});
            var Q3;
            Q3=makeQuery(id+"F5.boolean.opBoolean","COPY",EDGE,{"derivedFrom":makeQuery(id+"F5.opExtrude","SWEPT_EDGE",EDGE,{"disambiguationData":[OSD([sQuery(id+"F0.wireOp",EDGE,"E78"),sQuery(id+"F0.wireOp",EDGE,"E79")])]})});
            var Q4;
            Q4=makeQuery(id+"F5.boolean.opBoolean","COPY",EDGE,{"derivedFrom":makeQuery(id+"F5.opExtrude","SWEPT_EDGE",EDGE,{"disambiguationData":[OSD([sQuery(id+"F0.wireOp",EDGE,"E76"),sQuery(id+"F0.wireOp",EDGE,"E77")])]})});
            var Q5;
            Q5=makeQuery(id+"F5.boolean.opBoolean","COPY",EDGE,{"derivedFrom":makeQuery(id+"F5.opExtrude","SWEPT_EDGE",EDGE,{"disambiguationData":[OSD([sQuery(id+"F0.wireOp",EDGE,"E17"),sQuery(id+"F0.wireOp",EDGE,"E89")])]})});
            var Q6;
            Q6=makeQuery(id+"F5.boolean.opBoolean","COPY",EDGE,{"derivedFrom":makeQuery(id+"F5.opExtrude","SWEPT_EDGE",EDGE,{"disambiguationData":[OSD([sQuery(id+"F0.wireOp",EDGE,"E16"),sQuery(id+"F0.wireOp",EDGE,"E89")])]})});
            var Q7;
            Q7=makeQuery(id+"F5.boolean.opBoolean","COPY",EDGE,{"derivedFrom":makeQuery(id+"F5.opExtrude","SWEPT_EDGE",EDGE,{"disambiguationData":[OSD([sQuery(id+"F0.wireOp",EDGE,"E43"),sQuery(id+"F0.wireOp",EDGE,"E44")])]})});
            var Q8;
            Q8=makeQuery(id+"F5.boolean.opBoolean","COPY",EDGE,{"derivedFrom":makeQuery(id+"F5.opExtrude","SWEPT_EDGE",EDGE,{"disambiguationData":[OSD([sQuery(id+"F0.wireOp",EDGE,"E42"),sQuery(id+"F0.wireOp",EDGE,"E65")])]})});
            var Q9;
            Q9=makeQuery(id+"F5.boolean.opBoolean","COPY",EDGE,{"derivedFrom":makeQuery(id+"F5.opExtrude","SWEPT_EDGE",EDGE,{"disambiguationData":[OSD([sQuery(id+"F0.wireOp",EDGE,"E21"),sQuery(id+"F0.wireOp",EDGE,"E87")])]})});
            var Q10;
            Q10=makeQuery(id+"F5.boolean.opBoolean","COPY",EDGE,{"derivedFrom":makeQuery(id+"F5.opExtrude","SWEPT_EDGE",EDGE,{"disambiguationData":[OSD([sQuery(id+"F0.wireOp",EDGE,"E22"),sQuery(id+"F0.wireOp",EDGE,"E87")])]})});
            var Q11;
            Q11=makeQuery(id+"F5.boolean.opBoolean","COPY",EDGE,{"derivedFrom":makeQuery(id+"F5.opExtrude","SWEPT_EDGE",EDGE,{"disambiguationData":[OSD([sQuery(id+"F0.wireOp",EDGE,"E31"),sQuery(id+"F0.wireOp",EDGE,"E62")])]})});
            var Q12;
            Q12=makeQuery(id+"F5.boolean.opBoolean","COPY",EDGE,{"derivedFrom":makeQuery(id+"F5.opExtrude","SWEPT_EDGE",EDGE,{"disambiguationData":[OSD([sQuery(id+"F0.wireOp",EDGE,"E32"),sQuery(id+"F0.wireOp",EDGE,"E33")])]})});
            var Q13;
            Q13=makeQuery(id+"F5.boolean.opBoolean","COPY",EDGE,{"derivedFrom":makeQuery(id+"F5.opExtrude","SWEPT_EDGE",EDGE,{"disambiguationData":[OSD([sQuery(id+"F0.wireOp",EDGE,"E37"),sQuery(id+"F0.wireOp",EDGE,"E94")])]})});
            var Q14;
            Q14=makeQuery(id+"F5.boolean.opBoolean","COPY",EDGE,{"derivedFrom":makeQuery(id+"F5.opExtrude","SWEPT_EDGE",EDGE,{"disambiguationData":[OSD([sQuery(id+"F0.wireOp",EDGE,"E36"),sQuery(id+"F0.wireOp",EDGE,"E94")])]})});
            var Q15;
            Q15=makeQuery(id+"F5.boolean.opBoolean","COPY",EDGE,{"derivedFrom":makeQuery(id+"F5.opExtrude","SWEPT_EDGE",EDGE,{"disambiguationData":[OSD([sQuery(id+"F0.wireOp",EDGE,"E66"),sQuery(id+"F0.wireOp",EDGE,"E67")])]})});
            var Q16;
            Q16=makeQuery(id+"F5.boolean.opBoolean","COPY",EDGE,{"derivedFrom":makeQuery(id+"F5.opExtrude","SWEPT_EDGE",EDGE,{"disambiguationData":[OSD([sQuery(id+"F0.wireOp",EDGE,"E68"),sQuery(id+"F0.wireOp",EDGE,"E69")])]})});
            var Q17;
            Q17=makeQuery(id+"F5.boolean.opBoolean","COPY",EDGE,{"derivedFrom":makeQuery(id+"F5.opExtrude","SWEPT_EDGE",EDGE,{"disambiguationData":[OSD([sQuery(id+"F0.wireOp",EDGE,"E64"),sQuery(id+"F0.wireOp",EDGE,"E95")])]})});
            var Q18;
            Q18=makeQuery(id+"F5.boolean.opBoolean","COPY",EDGE,{"derivedFrom":makeQuery(id+"F5.opExtrude","SWEPT_EDGE",EDGE,{"disambiguationData":[OSD([sQuery(id+"F0.wireOp",EDGE,"E63"),sQuery(id+"F0.wireOp",EDGE,"E95")])]})});
            var Q19;
            Q19=makeQuery(id+"F5.boolean.opBoolean","COPY",EDGE,{"derivedFrom":makeQuery(id+"F5.opExtrude","SWEPT_EDGE",EDGE,{"disambiguationData":[OSD([sQuery(id+"F0.wireOp",EDGE,"E70"),sQuery(id+"F0.wireOp",EDGE,"E71")])]})});
            var Q20;
            Q20=makeQuery(id+"F5.boolean.opBoolean","COPY",EDGE,{"derivedFrom":makeQuery(id+"F5.opExtrude","SWEPT_EDGE",EDGE,{"disambiguationData":[OSD([sQuery(id+"F0.wireOp",EDGE,"E72"),sQuery(id+"F0.wireOp",EDGE,"E73")])]})});
            var Q21;
            Q21=makeQuery(id+"F5.boolean.opBoolean","COPY",EDGE,{"derivedFrom":makeQuery(id+"F5.opExtrude","SWEPT_EDGE",EDGE,{"disambiguationData":[OSD([sQuery(id+"F0.wireOp",EDGE,"E74"),sQuery(id+"F0.wireOp",EDGE,"E96")])]})});
            var Q22;
            Q22=makeQuery(id+"F5.boolean.opBoolean","COPY",EDGE,{"derivedFrom":makeQuery(id+"F5.opExtrude","SWEPT_EDGE",EDGE,{"disambiguationData":[OSD([sQuery(id+"F0.wireOp",EDGE,"E75"),sQuery(id+"F0.wireOp",EDGE,"E96")])]})});
            var Q23;
            Q23=makeQuery(id+"F5.boolean.opBoolean","COPY",EDGE,{"derivedFrom":makeQuery(id+"F5.opExtrude","SWEPT_EDGE",EDGE,{"disambiguationData":[OSD([sQuery(id+"F0.wireOp",EDGE,"E84"),sQuery(id+"F0.wireOp",EDGE,"E85")])]})});
            var Q24;
            Q24=makeQuery(id+"F5.boolean.opBoolean","COPY",EDGE,{"derivedFrom":makeQuery(id+"F5.opExtrude","SWEPT_EDGE",EDGE,{"disambiguationData":[OSD([sQuery(id+"F0.wireOp",EDGE,"E40"),sQuery(id+"F0.wireOp",EDGE,"E41")])]})});
            var Q25;
            Q25=makeQuery(id+"F5.boolean.opBoolean","COPY",EDGE,{"derivedFrom":makeQuery(id+"F5.opExtrude","SWEPT_EDGE",EDGE,{"disambiguationData":[OSD([sQuery(id+"F0.wireOp",EDGE,"E39"),sQuery(id+"F0.wireOp",EDGE,"E97")])]})});
            var Q26;
            Q26=makeQuery(id+"F5.boolean.opBoolean","COPY",EDGE,{"derivedFrom":makeQuery(id+"F5.opExtrude","SWEPT_EDGE",EDGE,{"disambiguationData":[OSD([sQuery(id+"F0.wireOp",EDGE,"E38"),sQuery(id+"F0.wireOp",EDGE,"E97")])]})});
            var Q27;
            Q27=makeQuery(id+"F5.boolean.opBoolean","COPY",EDGE,{"derivedFrom":makeQuery(id+"F5.opExtrude","SWEPT_EDGE",EDGE,{"disambiguationData":[OSD([sQuery(id+"F0.wireOp",EDGE,"E82"),sQuery(id+"F0.wireOp",EDGE,"E83")])]})});
            var Q28;
            Q28=makeQuery(id+"F5.boolean.opBoolean","COPY",EDGE,{"derivedFrom":makeQuery(id+"F5.opExtrude","SWEPT_EDGE",EDGE,{"disambiguationData":[OSD([sQuery(id+"F0.wireOp",EDGE,"E34"),sQuery(id+"F0.wireOp",EDGE,"E35")])]})});
            var Q29;
            Q29=makeQuery(id+"F5.boolean.opBoolean","COPY",EDGE,{"derivedFrom":makeQuery(id+"F5.opExtrude","SWEPT_EDGE",EDGE,{"disambiguationData":[OSD([sQuery(id+"F0.wireOp",EDGE,"E23"),sQuery(id+"F0.wireOp",EDGE,"E91")])]})});
            var Q30;
            Q30=makeQuery(id+"F5.boolean.opBoolean","COPY",EDGE,{"derivedFrom":makeQuery(id+"F5.opExtrude","SWEPT_EDGE",EDGE,{"disambiguationData":[OSD([sQuery(id+"F0.wireOp",EDGE,"E90"),sQuery(id+"F0.wireOp",EDGE,"E91")])]})});
            var Q31;
            Q31=makeQuery(id+"F5.boolean.opBoolean","COPY",EDGE,{"derivedFrom":makeQuery(id+"F5.opExtrude","SWEPT_EDGE",EDGE,{"disambiguationData":[OSD([sQuery(id+"F0.wireOp",EDGE,"E80"),sQuery(id+"F0.wireOp",EDGE,"E81")])]})});
            fillet(context, id + "F8", {"entities" : qUnion([Q0, Q1, Q2, Q3, Q4, Q5, Q6, Q7, Q8, Q9, Q10, Q11, Q12, Q13, Q14, Q15, Q16, Q17, Q18, Q19, Q20, Q21, Q22, Q23, Q24, Q25, Q26, Q27, Q28, Q29, Q30, Q31]), "radius" : 0.25 * mm, "tangentPropagation" : true, "defaultsChanged" : false, "vertexSettings" : [], "allowEdgeOverflow" : false});
        }
        {
            var Q0;
            Q0=makeQuery(id+"F2.opExtrude","CAP_FACE",FACE,{"disambiguationData":[OSD([sQuery(id+"F1.wireOp",EDGE,"E98")])],"isStart":true});
            var sketch = newSketch(context, id + "F9", { "sketchPlane" : qUnion([Q0])});
            skCircle(sketch, "E100", {"center": v(0, 0) * mm, "radius": 11 * mm});
            skCircle(sketch, "E101", {"center": v(0, 0) * mm, "radius": 8 * mm});
            skSolve(sketch);
        }
        {
            var Q0;
            Q0=makeQuery(id+"F9.imprint","IMPRINT",FACE,{"disambiguationData":[TD([[makeQuery(id+"F9.imprint","IMPRINT",EDGE,{"derivedFrom":sQuery(id+"F9.wireOp",EDGE,"E100")}),1.0]])]});
            extrude(context, id + "F10", {"entities" : qUnion([Q0]), "operationType" : NewBodyOperationType.ADD, "depth" : 10 * mm, "offsetDistance" : 25 * mm});
        }
        {
            var Q0;
            Q0=makeQuery(id+"F10.boolean.opBoolean","SPLIT",FACE,{"disambiguationData":[TD([makeQuery(id+"F10.opExtrude","SWEPT_FACE",FACE,{"disambiguationData":[OSD([sQuery(id+"F9.wireOp",EDGE,"E101")])]})])],"derivedFrom":makeQuery(id+"F2.opExtrude","CAP_FACE",FACE,{"disambiguationData":[OSD([sQuery(id+"F1.wireOp",EDGE,"E98")])],"isStart":true})});
            extrude(context, id + "F11", {"entities" : qUnion([Q0]), "operationType" : NewBodyOperationType.ADD, "depth" : 17 * mm, "offsetDistance" : 25 * mm});
        }
        {
            var Q0;
            Q0=makeQuery(id+"F11.opExtrude","CAP_FACE",FACE,{"disambiguationData":[OSD([sQuery(id+"F1.wireOp",EDGE,"E98")])],"isStart":false});
            var sketch = newSketch(context, id + "F12", { "sketchPlane" : qUnion([Q0])});
            skCircle(sketch, "E102", {"center": v(0, 0) * mm, "radius": 5 * mm});
            skLineSegment(sketch, "E103", {"start": v(-3, 4) * mm, "end": v(3, 4) * mm});
            skSolve(sketch);
        }
        {
            var Q0;
            {var subQ0=sQuery(id+"F12.wireOp",EDGE,"E103");Q0=makeQuery(id+"F12.imprint","IMPRINT",FACE,{"disambiguationData":[TD([[makeQuery(id+"F12.imprint","IMPRINT",EDGE,{"derivedFrom":subQ0}),-1.0]])]});}
            extrude(context, id + "F13", {"entities" : qUnion([Q0]), "operationType" : NewBodyOperationType.ADD, "depth" : 10 * mm, "offsetDistance" : 25 * mm});
        }
        {
            var Q0;
            Q0=makeQuery(id+"F4.opExtrude","CAP_FACE",FACE,{"disambiguationData":[OSD([sQuery(id+"F3.wireOp",EDGE,"E99.bottom"),sQuery(id+"F3.wireOp",EDGE,"E99.top"),sQuery(id+"F3.wireOp",EDGE,"E99.left"),sQuery(id+"F3.wireOp",EDGE,"E99.right")])],"isStart":false});
            var sketch = newSketch(context, id + "F14", { "sketchPlane" : qUnion([Q0])});
            skLineSegment(sketch, "E104.bottom", {"start": v(27.5, -27.5) * mm, "end": v(-27.5, -27.5) * mm, "construction": true});
            skLineSegment(sketch, "E104.top", {"start": v(27.5, 27.5) * mm, "end": v(-27.5, 27.5) * mm, "construction": true});
            skLineSegment(sketch, "E104.left", {"start": v(27.5, -27.5) * mm, "end": v(27.5, 27.5) * mm, "construction": true});
            skLineSegment(sketch, "E104.right", {"start": v(-27.5, -27.5) * mm, "end": v(-27.5, 27.5) * mm, "construction": true});
            skPoint(sketch, "E104.middle", {"position": v(0, 0) * mm});
            skSolve(sketch);
        }
        {
            var Q0;
            Q0=sQuery(id+"F14.wireOp",VERTEX,"E104.top.end");
            var Q1;
            Q1=sQuery(id+"F14.wireOp",VERTEX,"E104.bottom.end");
            var Q2;
            Q2=sQuery(id+"F14.wireOp",VERTEX,"E104.top.start");
            var Q3;
            Q3=sQuery(id+"F14.wireOp",VERTEX,"E104.bottom.start");
            var Q4;
            Q4=sQuery(id+"F14.wireOp",VERTEX,"E104.middle");
            var Q5;
            Q5=makeQuery(id+"F2.opExtrude","SWEPT_BODY",BODY,{"disambiguationData":[OSD([sQuery(id+"F1.wireOp",EDGE,"E98")])]});
            hole(context, id + "F15", {"style" : HoleStyle.C_BORE, "endStyle" : HoleEndStyle.THROUGH, "holeDiameter" : 4.5 * mm, "cBoreDiameter" : 15 * mm, "cBoreDepth" : 2 * mm, "majorDiameter" : 5 * mm, "isTappedThrough" : true, "tappedDepth" : 12 * mm, "tapClearance" : 3, "locations" : qUnion([Q0, Q1, Q2, Q3, Q4]), "scope" : qUnion([Q5])});
        }
        {
            var Q0;
            Q0=makeQuery(id+"F4.opExtrude","SWEPT_EDGE",EDGE,{"disambiguationData":[OSD([sQuery(id+"F3.wireOp",EDGE,"E99.top"),sQuery(id+"F3.wireOp",EDGE,"E99.left")])]});
            var Q1;
            Q1=makeQuery(id+"F4.opExtrude","SWEPT_EDGE",EDGE,{"disambiguationData":[OSD([sQuery(id+"F3.wireOp",EDGE,"E99.top"),sQuery(id+"F3.wireOp",EDGE,"E99.right")])]});
            var Q2;
            Q2=makeQuery(id+"F4.opExtrude","SWEPT_EDGE",EDGE,{"disambiguationData":[OSD([sQuery(id+"F3.wireOp",EDGE,"E99.bottom"),sQuery(id+"F3.wireOp",EDGE,"E99.right")])]});
            var Q3;
            Q3=makeQuery(id+"F4.opExtrude","SWEPT_EDGE",EDGE,{"disambiguationData":[OSD([sQuery(id+"F3.wireOp",EDGE,"E99.bottom"),sQuery(id+"F3.wireOp",EDGE,"E99.left")])]});
            fillet(context, id + "F16", {"entities" : qUnion([Q0, Q1, Q2, Q3]), "tangentPropagation" : true, "radius" : 5 * mm, "defaultsChanged" : false, "vertexSettings" : [], "allowEdgeOverflow" : false});
        }
        {
            var Q0;
            {var subQ0=sQuery(id+"F12.wireOp",EDGE,"E103");var subQ1=sQuery(id+"F12.wireOp",EDGE,"E102");Q0=makeQuery(id+"F13.opExtrude","SWEPT_EDGE",EDGE,{"disambiguationData":[OSD([subQ1,subQ0]),TDD([makeQuery(id+"F12.imprint","INTERSECT",VERTEX,{"disambiguationData":[OD(0.0)],"derivedFrom":[subQ1,subQ0]})])]});}
            var Q1;
            {var subQ0=sQuery(id+"F12.wireOp",EDGE,"E103");var subQ1=sQuery(id+"F12.wireOp",EDGE,"E102");Q1=makeQuery(id+"F13.opExtrude","SWEPT_EDGE",EDGE,{"disambiguationData":[OSD([subQ1,subQ0]),TDD([makeQuery(id+"F12.imprint","INTERSECT",VERTEX,{"disambiguationData":[OD(1.0)],"derivedFrom":[subQ1,subQ0]})])]});}
            fillet(context, id + "F17", {"entities" : qUnion([Q0, Q1]), "tangentPropagation" : true, "radius" : 2.5 * mm, "defaultsChanged" : true, "vertexSettings" : [], "allowEdgeOverflow" : false});
        }
        {
            var Q0;
            Q0=makeQuery(id+"F10.opExtrude","CAP_EDGE",EDGE,{"disambiguationData":[OSD([sQuery(id+"F9.wireOp",EDGE,"E100")])],"isStart":false});
            fillet(context, id + "F18", {"entities" : qUnion([Q0]), "tangentPropagation" : true, "radius" : 0.2 * mm, "defaultsChanged" : true, "vertexSettings" : [], "allowEdgeOverflow" : false});
        }
    });
